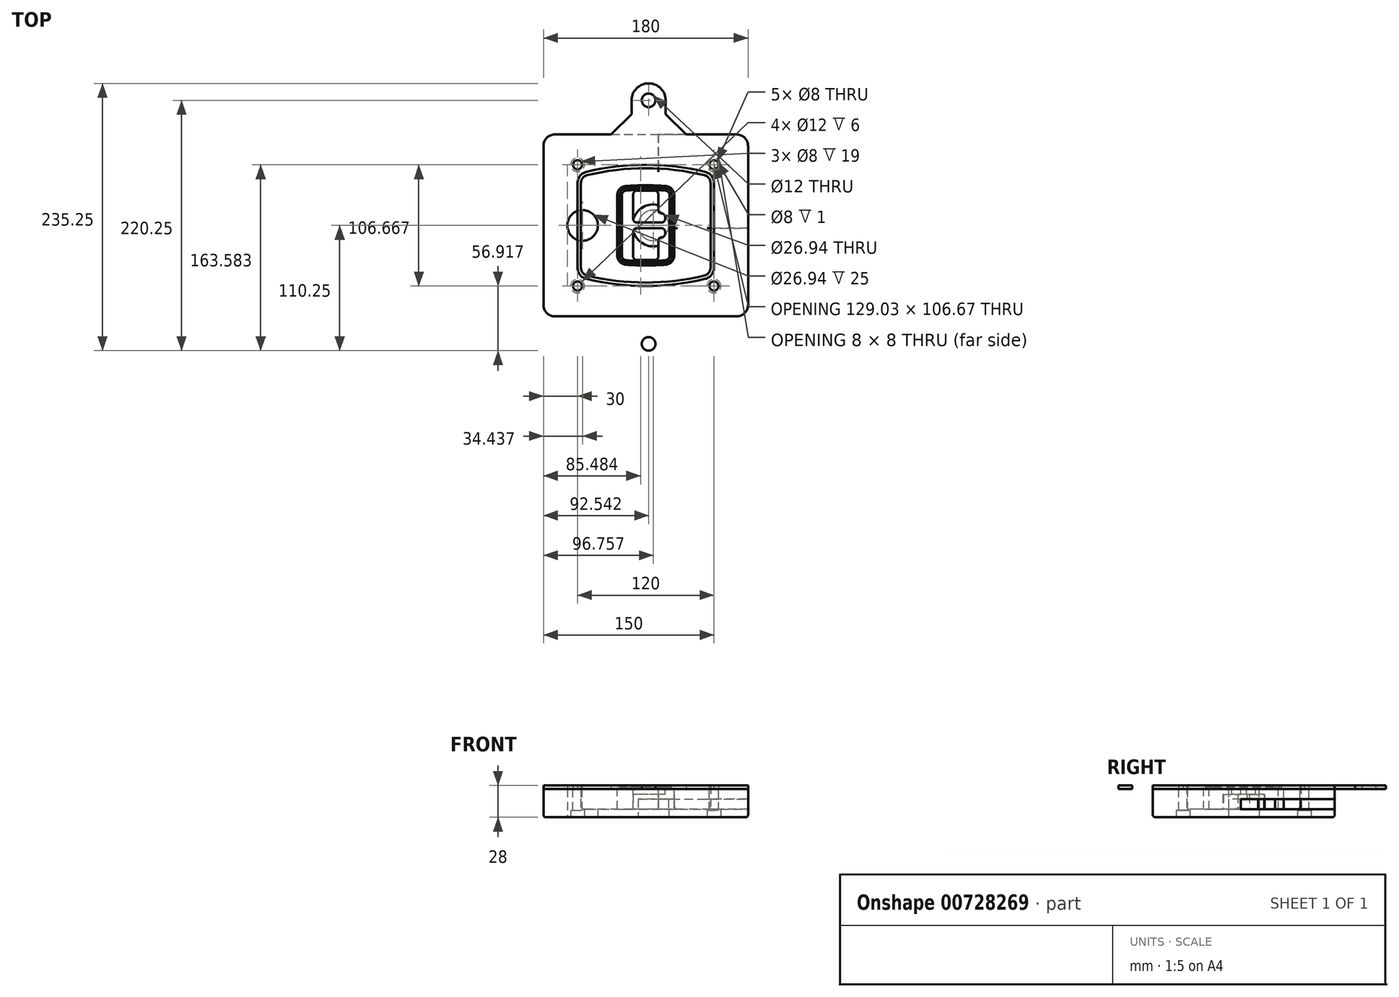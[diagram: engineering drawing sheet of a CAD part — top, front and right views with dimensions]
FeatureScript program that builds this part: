
annotation { "Feature Type Name" : "Feature", "Feature Type Description" : "" }
export const myFeature = defineFeature(function(context is Context, id is Id, definition is map)
    precondition{}
    {
        {
            var Q0;
            Q0=qCreatedBy(makeId("Top.planeOp"),FACE);
            var sketch = newSketch(context, id + "F0", { "sketchPlane" : qUnion([Q0])});
            skPoint(sketch, "E0.rect.middle", {"position": v(0, 0) * mm});
            skLineSegment(sketch, "E1.bottom", {"start": v(-80, -80) * mm, "end": v(80, -80) * mm});
            skLineSegment(sketch, "E1.top", {"start": v(-80, 80) * mm, "end": v(80, 80) * mm});
            skLineSegment(sketch, "E1.left", {"start": v(-90, -70) * mm, "end": v(-90, 70) * mm});
            skLineSegment(sketch, "E1.right", {"start": v(90, -70) * mm, "end": v(90, 70) * mm});
            skLineSegment(sketch, "E2", {"start": v(-90, 80) * mm, "end": v(90, -80) * mm, "construction": true});
            skLineSegment(sketch, "E3", {"start": v(90, 80) * mm, "end": v(-90, -80) * mm, "construction": true});
            skCircle(sketch, "E4", {"center": v(-60, 53.33) * mm, "radius": 4 * mm});
            skCircle(sketch, "E5", {"center": v(60, 53.33) * mm, "radius": 4 * mm});
            skCircle(sketch, "E6", {"center": v(60, -53.33) * mm, "radius": 4 * mm});
            skCircle(sketch, "E7", {"center": v(-60, -53.33) * mm, "radius": 4 * mm});
            skLineSegment(sketch, "E8", {"start": v(-60, 53.33) * mm, "end": v(60, 53.33) * mm, "construction": true});
            skLineSegment(sketch, "E9", {"start": v(60, 53.33) * mm, "end": v(60, -53.33) * mm, "construction": true});
            skLineSegment(sketch, "E10", {"start": v(60, -53.33) * mm, "end": v(-60, -53.33) * mm, "construction": true});
            skLineSegment(sketch, "E11", {"start": v(-60, -53.33) * mm, "end": v(-60, 53.33) * mm, "construction": true});
            skLineSegment(sketch, "E12", {"start": v(-60, 37.3) * mm, "end": v(-60, -37.3) * mm});
            skLineSegment(sketch, "E13", {"start": v(60, 37.3) * mm, "end": v(60, -37.3) * mm});
            skArc(sketch, "E14", {"start": v(52.38, 47.01) * mm, "mid": v(0, 53.33) * mm, "end": v(-52.38, 47.01) * mm});
            skArc(sketch, "E15", {"start": v(-52.38, -47.01) * mm, "mid": v(0, -53.33) * mm, "end": v(52.38, -47.01) * mm});
            skLineSegment(sketch, "E16", {"start": v(-60, 0) * mm, "end": v(60, 0) * mm, "construction": true});
            skPoint(sketch, "E17.visualSharp", {"position": v(-60, -45) * mm});
            skArc(sketch, "E17.filletArc", {"start": v(-60, -37.3) * mm, "mid": v(-57.87, -43.47) * mm, "end": v(-52.38, -47.01) * mm});
            skPoint(sketch, "E18.visualSharp", {"position": v(-60, 45) * mm});
            skArc(sketch, "E18.filletArc", {"start": v(-52.38, 47.01) * mm, "mid": v(-57.87, 43.47) * mm, "end": v(-60, 37.3) * mm});
            skPoint(sketch, "E19.visualSharp", {"position": v(60, 45) * mm});
            skArc(sketch, "E19.filletArc", {"start": v(60, 37.3) * mm, "mid": v(57.87, 43.47) * mm, "end": v(52.38, 47.01) * mm});
            skPoint(sketch, "E20.visualSharp", {"position": v(60, -45) * mm});
            skArc(sketch, "E20.filletArc", {"start": v(52.38, -47.01) * mm, "mid": v(57.87, -43.47) * mm, "end": v(60, -37.3) * mm});
            skPoint(sketch, "E21.visualSharp", {"position": v(-90, 80) * mm});
            skArc(sketch, "E21.filletArc", {"start": v(-80, 80) * mm, "mid": v(-87.07, 77.07) * mm, "end": v(-90, 70) * mm});
            skPoint(sketch, "E22.visualSharp", {"position": v(90, 80) * mm});
            skArc(sketch, "E22.filletArc", {"start": v(90, 70) * mm, "mid": v(87.07, 77.07) * mm, "end": v(80, 80) * mm});
            skPoint(sketch, "E23.visualSharp", {"position": v(90, -80) * mm});
            skArc(sketch, "E23.filletArc", {"start": v(80, -80) * mm, "mid": v(87.07, -77.07) * mm, "end": v(90, -70) * mm});
            skPoint(sketch, "E24.visualSharp", {"position": v(-90, -80) * mm});
            skArc(sketch, "E24.filletArc", {"start": v(-90, -70) * mm, "mid": v(-87.07, -77.07) * mm, "end": v(-80, -80) * mm});
            skArc(sketch, "E25.0", {"start": v(57, 37.3) * mm, "mid": v(55.5, 41.62) * mm, "end": v(51.67, 44.1) * mm});
            skLineSegment(sketch, "E25.1", {"start": v(57, 37.3) * mm, "end": v(57, -37.3) * mm});
            skArc(sketch, "E25.2", {"start": v(51.67, -44.1) * mm, "mid": v(55.5, -41.62) * mm, "end": v(57, -37.3) * mm});
            skArc(sketch, "E25.3", {"start": v(-51.67, -44.1) * mm, "mid": v(0, -50.33) * mm, "end": v(51.67, -44.1) * mm});
            skArc(sketch, "E25.4", {"start": v(-57, -37.3) * mm, "mid": v(-55.5, -41.62) * mm, "end": v(-51.67, -44.1) * mm});
            skArc(sketch, "E25.5", {"start": v(51.67, 44.1) * mm, "mid": v(0, 50.33) * mm, "end": v(-51.67, 44.1) * mm});
            skLineSegment(sketch, "E25.6", {"start": v(-57, 37.3) * mm, "end": v(-57, -37.3) * mm});
            skArc(sketch, "E25.7", {"start": v(-51.67, 44.1) * mm, "mid": v(-55.5, 41.62) * mm, "end": v(-57, 37.3) * mm});
            skArc(sketch, "E26.0", {"start": v(-53.33, 50.9) * mm, "mid": v(-61.01, 45.94) * mm, "end": v(-64, 37.3) * mm});
            skArc(sketch, "E26.1", {"start": v(53.33, 50.9) * mm, "mid": v(0, 57.33) * mm, "end": v(-53.33, 50.9) * mm});
            skArc(sketch, "E26.2", {"start": v(64, 37.3) * mm, "mid": v(61.01, 45.94) * mm, "end": v(53.33, 50.9) * mm});
            skLineSegment(sketch, "E26.3", {"start": v(64, 37.3) * mm, "end": v(64, -37.3) * mm});
            skArc(sketch, "E26.4", {"start": v(53.33, -50.9) * mm, "mid": v(61.01, -45.94) * mm, "end": v(64, -37.3) * mm});
            skLineSegment(sketch, "E26.5", {"start": v(-64, 37.3) * mm, "end": v(-64, -37.3) * mm});
            skArc(sketch, "E26.6", {"start": v(-53.33, -50.9) * mm, "mid": v(0, -57.33) * mm, "end": v(53.33, -50.9) * mm});
            skArc(sketch, "E26.7", {"start": v(-64, -37.3) * mm, "mid": v(-61.01, -45.94) * mm, "end": v(-53.33, -50.9) * mm});
            skSolve(sketch);
        }
        {
            var Q0;
            Q0=makeQuery(id+"F0.imprint","IMPRINT",FACE,{"disambiguationData":[TD([[makeQuery(id+"F0.imprint","IMPRINT",EDGE,{"derivedFrom":sQuery(id+"F0.wireOp",EDGE,"E1.bottom")}),1.0]])]});
            var Q1;
            Q1=makeQuery(id+"F0.imprint","IMPRINT",FACE,{"disambiguationData":[TD([[makeQuery(id+"F0.imprint","IMPRINT",EDGE,{"derivedFrom":sQuery(id+"F0.wireOp",EDGE,"E12")}),1.0]])]});
            var Q2;
            Q2=makeQuery(id+"F0.imprint","IMPRINT",FACE,{"disambiguationData":[TD([[makeQuery(id+"F0.imprint","IMPRINT",EDGE,{"derivedFrom":sQuery(id+"F0.wireOp",EDGE,"E25.0")}),1.0]])]});
            var Q3;
            Q3=makeQuery(id+"F0.imprint","IMPRINT",FACE,{"disambiguationData":[TD([[makeQuery(id+"F0.imprint","IMPRINT",EDGE,{"derivedFrom":sQuery(id+"F0.wireOp",EDGE,"E12")}),-1.0]])]});
            extrude(context, id + "F1", {"entities" : qUnion([Q0, Q1, Q2, Q3]), "oppositeDirection" : true, "depth" : 25 * mm, "offsetDistance" : 25 * mm});
        }
        {
            var Q0;
            Q0=makeQuery(id+"F0.imprint","IMPRINT",FACE,{"disambiguationData":[TD([[makeQuery(id+"F0.imprint","IMPRINT",EDGE,{"derivedFrom":sQuery(id+"F0.wireOp",EDGE,"E12")}),1.0]])]});
            extrude(context, id + "F2", {"entities" : qUnion([Q0]), "operationType" : NewBodyOperationType.ADD, "depth" : 3 * mm});
        }
        {
            var Q0;
            Q0=makeQuery(id+"F0.imprint","IMPRINT",FACE,{"disambiguationData":[TD([[makeQuery(id+"F0.imprint","IMPRINT",EDGE,{"derivedFrom":sQuery(id+"F0.wireOp",EDGE,"E25.0")}),1.0]])]});
            extrude(context, id + "F3", {"entities" : qUnion([Q0]), "operationType" : NewBodyOperationType.REMOVE, "oppositeDirection" : true, "depth" : 18 * mm});
        }
        {
            var Q0;
            Q0=makeQuery(id+"F2.opExtrude","CAP_FACE",FACE,{"disambiguationData":[OSD([sQuery(id+"F0.wireOp",EDGE,"E12"),sQuery(id+"F0.wireOp",EDGE,"E13"),sQuery(id+"F0.wireOp",EDGE,"E14"),sQuery(id+"F0.wireOp",EDGE,"E15"),sQuery(id+"F0.wireOp",EDGE,"E17.filletArc"),sQuery(id+"F0.wireOp",EDGE,"E18.filletArc"),sQuery(id+"F0.wireOp",EDGE,"E19.filletArc"),sQuery(id+"F0.wireOp",EDGE,"E20.filletArc"),sQuery(id+"F0.wireOp",EDGE,"E25.0"),sQuery(id+"F0.wireOp",EDGE,"E25.1"),sQuery(id+"F0.wireOp",EDGE,"E25.2"),sQuery(id+"F0.wireOp",EDGE,"E25.3"),sQuery(id+"F0.wireOp",EDGE,"E25.4"),sQuery(id+"F0.wireOp",EDGE,"E25.5"),sQuery(id+"F0.wireOp",EDGE,"E25.6"),sQuery(id+"F0.wireOp",EDGE,"E25.7")])],"isStart":false});
            var sketch = newSketch(context, id + "F4", { "sketchPlane" : qUnion([Q0])});
            skArc(sketch, "E27.0", {"start": v(-17.7, -34.56) * mm, "mid": v(0, -35.33) * mm, "end": v(17.7, -34.56) * mm});
            skArc(sketch, "E28.0", {"start": v(17.7, 34.56) * mm, "mid": v(0, 35.33) * mm, "end": v(-17.7, 34.56) * mm});
            skLineSegment(sketch, "E29", {"start": v(-25, 26.59) * mm, "end": v(-25, -26.59) * mm});
            skLineSegment(sketch, "E30", {"start": v(25, 26.59) * mm, "end": v(25, -26.59) * mm});
            skLineSegment(sketch, "E31", {"start": v(-25, 33.78) * mm, "end": v(25, 33.78) * mm, "construction": true});
            skLineSegment(sketch, "E32", {"start": v(-25, -33.78) * mm, "end": v(25, -33.78) * mm, "construction": true});
            skPoint(sketch, "E33.visualSharp", {"position": v(-25, 33.78) * mm});
            skArc(sketch, "E33.filletArc", {"start": v(-17.7, 34.56) * mm, "mid": v(-22.9, 32) * mm, "end": v(-25, 26.59) * mm});
            skPoint(sketch, "E34.visualSharp", {"position": v(25, 33.78) * mm});
            skArc(sketch, "E34.filletArc", {"start": v(25, 26.59) * mm, "mid": v(22.9, 32) * mm, "end": v(17.7, 34.56) * mm});
            skPoint(sketch, "E35.visualSharp", {"position": v(25, -33.78) * mm});
            skArc(sketch, "E35.filletArc", {"start": v(17.7, -34.56) * mm, "mid": v(22.9, -32) * mm, "end": v(25, -26.59) * mm});
            skPoint(sketch, "E36.visualSharp", {"position": v(-25, -33.78) * mm});
            skArc(sketch, "E36.filletArc", {"start": v(-25, -26.59) * mm, "mid": v(-22.9, -32) * mm, "end": v(-17.7, -34.56) * mm});
            skArc(sketch, "E37.0", {"start": v(51.67, 44.1) * mm, "mid": v(0, 50.33) * mm, "end": v(-51.67, 44.1) * mm});
            skArc(sketch, "E37.1", {"start": v(-51.67, 44.1) * mm, "mid": v(-55.5, 41.62) * mm, "end": v(-57, 37.3) * mm});
            skLineSegment(sketch, "E37.2", {"start": v(-57, 37.3) * mm, "end": v(-57, -37.3) * mm});
            skArc(sketch, "E37.3", {"start": v(-57, -37.3) * mm, "mid": v(-55.5, -41.62) * mm, "end": v(-51.67, -44.1) * mm});
            skArc(sketch, "E37.4", {"start": v(-51.67, -44.1) * mm, "mid": v(0, -50.33) * mm, "end": v(51.67, -44.1) * mm});
            skArc(sketch, "E37.5", {"start": v(51.67, -44.1) * mm, "mid": v(55.5, -41.62) * mm, "end": v(57, -37.3) * mm});
            skLineSegment(sketch, "E37.6", {"start": v(57, 37.3) * mm, "end": v(57, -37.3) * mm});
            skArc(sketch, "E37.7", {"start": v(57, 37.3) * mm, "mid": v(55.5, 41.62) * mm, "end": v(51.67, 44.1) * mm});
            skLineSegment(sketch, "E38.0", {"start": v(23, 26.59) * mm, "end": v(23, -26.59) * mm});
            skArc(sketch, "E38.1", {"start": v(17.53, -32.56) * mm, "mid": v(21.42, -30.64) * mm, "end": v(23, -26.59) * mm});
            skArc(sketch, "E38.2", {"start": v(-17.53, -32.56) * mm, "mid": v(0, -33.33) * mm, "end": v(17.53, -32.56) * mm});
            skArc(sketch, "E38.3", {"start": v(-23, -26.59) * mm, "mid": v(-21.42, -30.64) * mm, "end": v(-17.53, -32.56) * mm});
            skLineSegment(sketch, "E38.4", {"start": v(-23, 26.59) * mm, "end": v(-23, -26.59) * mm});
            skArc(sketch, "E38.5", {"start": v(23, 26.59) * mm, "mid": v(21.42, 30.64) * mm, "end": v(17.53, 32.56) * mm});
            skArc(sketch, "E38.6", {"start": v(-17.53, 32.56) * mm, "mid": v(-21.42, 30.64) * mm, "end": v(-23, 26.59) * mm});
            skArc(sketch, "E38.7", {"start": v(17.53, 32.56) * mm, "mid": v(0, 33.33) * mm, "end": v(-17.53, 32.56) * mm});
            skArc(sketch, "E39.0", {"start": v(21, 26.59) * mm, "mid": v(19.95, 29.29) * mm, "end": v(17.35, 30.57) * mm});
            skLineSegment(sketch, "E39.1", {"start": v(21, 26.59) * mm, "end": v(21, -26.59) * mm});
            skArc(sketch, "E39.2", {"start": v(17.35, -30.57) * mm, "mid": v(19.95, -29.29) * mm, "end": v(21, -26.59) * mm});
            skArc(sketch, "E39.3", {"start": v(-17.35, -30.57) * mm, "mid": v(0, -31.33) * mm, "end": v(17.35, -30.57) * mm});
            skArc(sketch, "E39.4", {"start": v(-21, -26.59) * mm, "mid": v(-19.95, -29.29) * mm, "end": v(-17.35, -30.57) * mm});
            skArc(sketch, "E39.5", {"start": v(17.35, 30.57) * mm, "mid": v(0, 31.33) * mm, "end": v(-17.35, 30.57) * mm});
            skLineSegment(sketch, "E39.6", {"start": v(-21, 26.59) * mm, "end": v(-21, -26.59) * mm});
            skArc(sketch, "E39.7", {"start": v(-17.35, 30.57) * mm, "mid": v(-19.95, 29.29) * mm, "end": v(-21, 26.59) * mm});
            skLineSegment(sketch, "E40", {"start": v(-25, 0) * mm, "end": v(25, 0) * mm, "construction": true});
            skLineSegment(sketch, "E41", {"start": v(-11, 5.5) * mm, "end": v(-11, 27.5) * mm});
            skLineSegment(sketch, "E42", {"start": v(-8, 30.5) * mm, "end": v(8, 30.5) * mm});
            skLineSegment(sketch, "E43", {"start": v(11, 27.5) * mm, "end": v(11, 13.5) * mm});
            skLineSegment(sketch, "E44", {"start": v(14, 10.5) * mm, "end": v(14, 10.5) * mm});
            skLineSegment(sketch, "E45", {"start": v(17, 7.5) * mm, "end": v(17, 5.5) * mm});
            skLineSegment(sketch, "E46", {"start": v(14, 2.5) * mm, "end": v(-8, 2.5) * mm});
            skPoint(sketch, "E47.visualSharp", {"position": v(-11, 30.5) * mm});
            skArc(sketch, "E47.filletArc", {"start": v(-8, 30.5) * mm, "mid": v(-10.12, 29.62) * mm, "end": v(-11, 27.5) * mm});
            skPoint(sketch, "E48.visualSharp", {"position": v(11, 30.5) * mm});
            skArc(sketch, "E48.filletArc", {"start": v(11, 27.5) * mm, "mid": v(10.12, 29.62) * mm, "end": v(8, 30.5) * mm});
            skPoint(sketch, "E49.visualSharp", {"position": v(11, 10.5) * mm});
            skArc(sketch, "E49.filletArc", {"start": v(11, 13.5) * mm, "mid": v(11.88, 11.38) * mm, "end": v(14, 10.5) * mm});
            skPoint(sketch, "E50.visualSharp", {"position": v(17, 10.5) * mm});
            skArc(sketch, "E50.filletArc", {"start": v(17, 7.5) * mm, "mid": v(16.12, 9.62) * mm, "end": v(14, 10.5) * mm});
            skPoint(sketch, "E51.visualSharp", {"position": v(17, 2.5) * mm});
            skArc(sketch, "E51.filletArc", {"start": v(14, 2.5) * mm, "mid": v(16.12, 3.38) * mm, "end": v(17, 5.5) * mm});
            skPoint(sketch, "E52.visualSharp", {"position": v(-11, 2.5) * mm});
            skArc(sketch, "E52.filletArc", {"start": v(-11, 5.5) * mm, "mid": v(-10.12, 3.38) * mm, "end": v(-8, 2.5) * mm});
            skLineSegment(sketch, "E53.0.MirrorCS", {"start": v(14, -2.5) * mm, "end": v(-8, -2.5) * mm});
            skArc(sketch, "E54.0.MirrorCS", {"start": v(-11, -5.5) * mm, "mid": v(-10.12, -3.38) * mm, "end": v(-8, -2.5) * mm});
            skLineSegment(sketch, "E55.0.MirrorCS", {"start": v(-11, -5.5) * mm, "end": v(-11, -27.5) * mm});
            skArc(sketch, "E56.0.MirrorCS", {"start": v(-8, -30.5) * mm, "mid": v(-10.12, -29.62) * mm, "end": v(-11, -27.5) * mm});
            skLineSegment(sketch, "E57.0.MirrorCS", {"start": v(-8, -30.5) * mm, "end": v(8, -30.5) * mm});
            skArc(sketch, "E58.0.MirrorCS", {"start": v(11, -27.5) * mm, "mid": v(10.12, -29.62) * mm, "end": v(8, -30.5) * mm});
            skLineSegment(sketch, "E59.0.MirrorCS", {"start": v(11, -27.5) * mm, "end": v(11, -13.5) * mm});
            skArc(sketch, "E60.0.MirrorCS", {"start": v(11, -13.5) * mm, "mid": v(11.88, -11.38) * mm, "end": v(14, -10.5) * mm});
            skArc(sketch, "E61.0.MirrorCS", {"start": v(17, -7.5) * mm, "mid": v(16.12, -9.62) * mm, "end": v(14, -10.5) * mm});
            skLineSegment(sketch, "E62.0.MirrorCS", {"start": v(17, -7.5) * mm, "end": v(17, -5.5) * mm});
            skArc(sketch, "E63.0.MirrorCS", {"start": v(14, -2.5) * mm, "mid": v(16.12, -3.38) * mm, "end": v(17, -5.5) * mm});
            skSolve(sketch);
        }
        {
            var Q0;
            Q0=makeQuery(id+"F4.imprint","IMPRINT",FACE,{"disambiguationData":[TD([[makeQuery(id+"F4.imprint","IMPRINT",EDGE,{"derivedFrom":sQuery(id+"F4.wireOp",EDGE,"E27.0")}),1.0]])]});
            var Q1;
            Q1=makeQuery(id+"F4.imprint","IMPRINT",FACE,{"disambiguationData":[TD([[makeQuery(id+"F4.imprint","IMPRINT",EDGE,{"derivedFrom":sQuery(id+"F4.wireOp",EDGE,"E38.0")}),-1.0]])]});
            var Q2;
            Q2=makeQuery(id+"F4.imprint","IMPRINT",FACE,{"disambiguationData":[TD([[makeQuery(id+"F4.imprint","IMPRINT",EDGE,{"derivedFrom":sQuery(id+"F4.wireOp",EDGE,"E39.0")}),1.0]])]});
            extrude(context, id + "F5", {"entities" : qUnion([Q0, Q1, Q2]), "operationType" : NewBodyOperationType.ADD, "endBound" : BoundingType.UP_TO_NEXT, "oppositeDirection" : true, "depth" : 25 * mm});
        }
        {
            var Q0;
            Q0=makeQuery(id+"F4.imprint","IMPRINT",FACE,{"disambiguationData":[TD([[makeQuery(id+"F4.imprint","IMPRINT",EDGE,{"derivedFrom":sQuery(id+"F4.wireOp",EDGE,"E38.0")}),-1.0]])]});
            extrude(context, id + "F6", {"entities" : qUnion([Q0]), "operationType" : NewBodyOperationType.REMOVE, "oppositeDirection" : true, "depth" : 2 * mm});
        }
        {
            var Q0;
            Q0=makeQuery(id+"F1.opExtrude","CAP_FACE",FACE,{"disambiguationData":[OSD([sQuery(id+"F0.wireOp",EDGE,"E1.bottom"),sQuery(id+"F0.wireOp",EDGE,"E1.top"),sQuery(id+"F0.wireOp",EDGE,"E1.left"),sQuery(id+"F0.wireOp",EDGE,"E1.right"),sQuery(id+"F0.wireOp",EDGE,"E4"),sQuery(id+"F0.wireOp",EDGE,"E5"),sQuery(id+"F0.wireOp",EDGE,"E6"),sQuery(id+"F0.wireOp",EDGE,"E7"),sQuery(id+"F0.wireOp",EDGE,"E21.filletArc"),sQuery(id+"F0.wireOp",EDGE,"E22.filletArc"),sQuery(id+"F0.wireOp",EDGE,"E23.filletArc"),sQuery(id+"F0.wireOp",EDGE,"E24.filletArc")])],"isStart":false});
            var sketch = newSketch(context, id + "F7", { "sketchPlane" : qUnion([Q0])});
            skCircle(sketch, "E64", {"center": v(6.76, 0) * mm, "radius": 13.47 * mm});
            skCircle(sketch, "E65", {"center": v(-55.56, 0) * mm, "radius": 13.47 * mm});
            skLineSegment(sketch, "E66", {"start": v(90, 0) * mm, "end": v(-90, 0) * mm});
            skCircle(sketch, "E67", {"center": v(6.76, 0) * mm, "radius": 18.47 * mm});
            skCircle(sketch, "E68", {"center": v(60, -53.33) * mm, "radius": 6 * mm});
            skCircle(sketch, "E69", {"center": v(-60, -53.33) * mm, "radius": 6 * mm});
            skCircle(sketch, "E70", {"center": v(-60, 53.33) * mm, "radius": 6 * mm});
            skCircle(sketch, "E71", {"center": v(60, 53.33) * mm, "radius": 6 * mm});
            skSolve(sketch);
        }
        {
            var Q0;
            {var subQ1=sQuery(id+"F7.wireOp",EDGE,"E66");var subQ4=sQuery(id+"F7.wireOp",EDGE,"E64");var subQ6=makeQuery(id+"F7.imprint","INTERSECT",VERTEX,{"disambiguationData":[OD(0.0)],"derivedFrom":[subQ4,subQ1]});Q0=makeQuery(id+"F7.imprint","IMPRINT",FACE,{"disambiguationData":[TD([[makeQuery(id+"F7.imprint","IMPRINT",EDGE,{"disambiguationData":[TD([[subQ6,-1.0]])],"derivedFrom":subQ4}),-1.0]])]});}
            var Q1;
            {var subQ0=sQuery(id+"F7.wireOp",EDGE,"E66");var subQ1=sQuery(id+"F7.wireOp",EDGE,"E64");var subQ3=makeQuery(id+"F7.imprint","INTERSECT",VERTEX,{"disambiguationData":[OD(0.0)],"derivedFrom":[subQ1,subQ0]});Q1=makeQuery(id+"F7.imprint","IMPRINT",FACE,{"disambiguationData":[TD([[makeQuery(id+"F7.imprint","IMPRINT",EDGE,{"disambiguationData":[TD([[subQ3,-1.0]])],"derivedFrom":subQ1}),1.0]])]});}
            var Q2;
            {var subQ0=sQuery(id+"F7.wireOp",EDGE,"E66");var subQ1=sQuery(id+"F7.wireOp",EDGE,"E64");var subQ3=makeQuery(id+"F7.imprint","INTERSECT",VERTEX,{"disambiguationData":[OD(0.0)],"derivedFrom":[subQ1,subQ0]});Q2=makeQuery(id+"F7.imprint","IMPRINT",FACE,{"disambiguationData":[TD([[makeQuery(id+"F7.imprint","IMPRINT",EDGE,{"disambiguationData":[TD([[subQ3,1.0]])],"derivedFrom":subQ1}),1.0]])]});}
            var Q3;
            {var subQ1=sQuery(id+"F7.wireOp",EDGE,"E66");var subQ4=sQuery(id+"F7.wireOp",EDGE,"E64");var subQ6=makeQuery(id+"F7.imprint","INTERSECT",VERTEX,{"disambiguationData":[OD(0.0)],"derivedFrom":[subQ4,subQ1]});Q3=makeQuery(id+"F7.imprint","IMPRINT",FACE,{"disambiguationData":[TD([[makeQuery(id+"F7.imprint","IMPRINT",EDGE,{"disambiguationData":[TD([[subQ6,1.0]])],"derivedFrom":subQ4}),-1.0]])]});}
            extrude(context, id + "F8", {"entities" : qUnion([Q0, Q1, Q2, Q3]), "operationType" : NewBodyOperationType.ADD, "oppositeDirection" : true, "depth" : 20 * mm});
        }
        {
            var Q0;
            {var subQ0=sQuery(id+"F7.wireOp",EDGE,"E66");var subQ1=sQuery(id+"F7.wireOp",EDGE,"E64");var subQ3=makeQuery(id+"F7.imprint","INTERSECT",VERTEX,{"disambiguationData":[OD(0.0)],"derivedFrom":[subQ1,subQ0]});Q0=makeQuery(id+"F7.imprint","IMPRINT",FACE,{"disambiguationData":[TD([[makeQuery(id+"F7.imprint","IMPRINT",EDGE,{"disambiguationData":[TD([[subQ3,-1.0]])],"derivedFrom":subQ1}),1.0]])]});}
            var Q1;
            {var subQ0=sQuery(id+"F7.wireOp",EDGE,"E66");var subQ1=sQuery(id+"F7.wireOp",EDGE,"E64");var subQ3=makeQuery(id+"F7.imprint","INTERSECT",VERTEX,{"disambiguationData":[OD(0.0)],"derivedFrom":[subQ1,subQ0]});Q1=makeQuery(id+"F7.imprint","IMPRINT",FACE,{"disambiguationData":[TD([[makeQuery(id+"F7.imprint","IMPRINT",EDGE,{"disambiguationData":[TD([[subQ3,1.0]])],"derivedFrom":subQ1}),1.0]])]});}
            extrude(context, id + "F9", {"entities" : qUnion([Q0, Q1]), "operationType" : NewBodyOperationType.REMOVE, "oppositeDirection" : true, "depth" : 16 * mm});
        }
        {
            var Q0;
            {var subQ0=sQuery(id+"F7.wireOp",EDGE,"E66");var subQ1=sQuery(id+"F7.wireOp",EDGE,"E65");var subQ3=makeQuery(id+"F7.imprint","INTERSECT",VERTEX,{"disambiguationData":[OD(0.0)],"derivedFrom":[subQ1,subQ0]});Q0=makeQuery(id+"F7.imprint","IMPRINT",FACE,{"disambiguationData":[TD([[makeQuery(id+"F7.imprint","IMPRINT",EDGE,{"disambiguationData":[TD([[subQ3,-1.0]])],"derivedFrom":subQ1}),1.0]])]});}
            var Q1;
            {var subQ0=sQuery(id+"F7.wireOp",EDGE,"E66");var subQ1=sQuery(id+"F7.wireOp",EDGE,"E65");var subQ3=makeQuery(id+"F7.imprint","INTERSECT",VERTEX,{"disambiguationData":[OD(0.0)],"derivedFrom":[subQ1,subQ0]});Q1=makeQuery(id+"F7.imprint","IMPRINT",FACE,{"disambiguationData":[TD([[makeQuery(id+"F7.imprint","IMPRINT",EDGE,{"disambiguationData":[TD([[subQ3,1.0]])],"derivedFrom":subQ1}),1.0]])]});}
            extrude(context, id + "F10", {"entities" : qUnion([Q0, Q1]), "operationType" : NewBodyOperationType.REMOVE, "oppositeDirection" : true, "depth" : 25 * mm});
        }
        {
            var Q0;
            Q0=makeQuery(id+"F7.imprint","IMPRINT",FACE,{"disambiguationData":[TD([[makeQuery(id+"F7.imprint","IMPRINT",EDGE,{"derivedFrom":sQuery(id+"F7.wireOp",EDGE,"E68")}),1.0]])]});
            var Q1;
            Q1=makeQuery(id+"F7.imprint","IMPRINT",FACE,{"disambiguationData":[TD([[makeQuery(id+"F7.imprint","IMPRINT",EDGE,{"derivedFrom":makeQuery(id+"F1.opExtrude","CAP_EDGE",EDGE,{"disambiguationData":[OSD([sQuery(id+"F0.wireOp",EDGE,"E5")])],"isStart":false})}),-1.0]])]});
            var Q2;
            Q2=makeQuery(id+"F7.imprint","IMPRINT",FACE,{"disambiguationData":[TD([[makeQuery(id+"F7.imprint","IMPRINT",EDGE,{"derivedFrom":sQuery(id+"F7.wireOp",EDGE,"E69")}),1.0]])]});
            var Q3;
            Q3=makeQuery(id+"F7.imprint","IMPRINT",FACE,{"disambiguationData":[TD([[makeQuery(id+"F7.imprint","IMPRINT",EDGE,{"derivedFrom":makeQuery(id+"F1.opExtrude","CAP_EDGE",EDGE,{"disambiguationData":[OSD([sQuery(id+"F0.wireOp",EDGE,"E4")])],"isStart":false})}),-1.0]])]});
            var Q4;
            Q4=makeQuery(id+"F7.imprint","IMPRINT",FACE,{"disambiguationData":[TD([[makeQuery(id+"F7.imprint","IMPRINT",EDGE,{"derivedFrom":sQuery(id+"F7.wireOp",EDGE,"E70")}),1.0]])]});
            var Q5;
            Q5=makeQuery(id+"F7.imprint","IMPRINT",FACE,{"disambiguationData":[TD([[makeQuery(id+"F7.imprint","IMPRINT",EDGE,{"derivedFrom":makeQuery(id+"F1.opExtrude","CAP_EDGE",EDGE,{"disambiguationData":[OSD([sQuery(id+"F0.wireOp",EDGE,"E7")])],"isStart":false})}),-1.0]])]});
            var Q6;
            Q6=makeQuery(id+"F7.imprint","IMPRINT",FACE,{"disambiguationData":[TD([[makeQuery(id+"F7.imprint","IMPRINT",EDGE,{"derivedFrom":sQuery(id+"F7.wireOp",EDGE,"E71")}),1.0]])]});
            var Q7;
            Q7=makeQuery(id+"F7.imprint","IMPRINT",FACE,{"disambiguationData":[TD([[makeQuery(id+"F7.imprint","IMPRINT",EDGE,{"derivedFrom":makeQuery(id+"F1.opExtrude","CAP_EDGE",EDGE,{"disambiguationData":[OSD([sQuery(id+"F0.wireOp",EDGE,"E6")])],"isStart":false})}),-1.0]])]});
            extrude(context, id + "F11", {"entities" : qUnion([Q0, Q1, Q2, Q3, Q4, Q5, Q6, Q7]), "operationType" : NewBodyOperationType.REMOVE, "oppositeDirection" : true, "depth" : 6 * mm});
        }
        {
            var Q0;
            Q0=makeQuery(id+"F9.boolean.opBoolean","COPY",FACE,{"derivedFrom":makeQuery(id+"F9.opExtrude","CAP_FACE",FACE,{"disambiguationData":[OSD([sQuery(id+"F7.wireOp",EDGE,"E64")])],"isStart":false})});
            var sketch = newSketch(context, id + "F12", { "sketchPlane" : qUnion([Q0])});
            skArc(sketch, "E72.0", {"start": v(11, -88.19) * mm, "mid": v(97.1, -83.6) * mm, "end": v(92.5, 2.5) * mm});
            skLineSegment(sketch, "E72.1", {"start": v(11, -17.97) * mm, "end": v(11, -17.97) * mm});
            skLineSegment(sketch, "E73", {"start": v(92.5, -105.13) * mm, "end": v(102.3, -105.13) * mm});
            skLineSegment(sketch, "E74.0", {"start": v(92.5, 2.5) * mm, "end": v(14, 2.5) * mm});
            skArc(sketch, "E74.1", {"start": v(14, 2.5) * mm, "mid": v(16.12, 3.38) * mm, "end": v(17, 5.5) * mm});
            skLineSegment(sketch, "E74.2", {"start": v(17, 7.5) * mm, "end": v(17, 5.5) * mm});
            skArc(sketch, "E74.3", {"start": v(17, 7.5) * mm, "mid": v(16.12, 9.62) * mm, "end": v(14, 10.5) * mm});
            skArc(sketch, "E74.4", {"start": v(11, 13.5) * mm, "mid": v(11.88, 11.38) * mm, "end": v(14, 10.5) * mm});
            skLineSegment(sketch, "E74.5", {"start": v(11, 13.5) * mm, "end": v(11, -88.19) * mm});
            skLineSegment(sketch, "E74.7", {"start": v(92.5, -2.5) * mm, "end": v(14, -2.5) * mm});
            skArc(sketch, "E74.8", {"start": v(14, -2.5) * mm, "mid": v(16.12, -3.38) * mm, "end": v(17, -5.5) * mm});
            skLineSegment(sketch, "E74.9", {"start": v(17, -7.5) * mm, "end": v(17, -5.5) * mm});
            skArc(sketch, "E74.10", {"start": v(17, -7.5) * mm, "mid": v(16.12, -9.62) * mm, "end": v(14, -10.5) * mm});
            skArc(sketch, "E74.11", {"start": v(11, -13.5) * mm, "mid": v(11.88, -11.38) * mm, "end": v(14, -10.5) * mm});
            skLineSegment(sketch, "E74.12", {"start": v(11, -17.97) * mm, "end": v(11, -13.5) * mm});
            skPoint(sketch, "E75.orphan", {"position": v(11, -27.5) * mm});
            skPoint(sketch, "E76.orphan", {"position": v(-8, -2.5) * mm});
            skPoint(sketch, "E77.orphan", {"position": v(-8, 2.5) * mm});
            skPoint(sketch, "E78.orphan", {"position": v(11, 27.5) * mm});
            skSolve(sketch);
        }
        {
            var Q0;
            {var subQ7=sQuery(id+"F12.wireOp",EDGE,"E72.0");var subQ14=sQuery(id+"F12.wireOp",EDGE,"E72.1");var subQ16=sQuery(id+"F12.wireOp",EDGE,"E74.1");var subQ18=sQuery(id+"F12.wireOp",EDGE,"E74.8");Q0=qUnion([makeQuery(id+"F12.imprint","IMPRINT",FACE,{"disambiguationData":[TD([[makeQuery(id+"F12.imprint","IMPRINT",EDGE,{"derivedFrom":subQ7}),1.0]])]}),makeQuery(id+"F12.imprint","IMPRINT",FACE,{"disambiguationData":[TD([[makeQuery(id+"F12.imprint","IMPRINT",EDGE,{"derivedFrom":subQ14}),1.0]])]}),makeQuery(id+"F12.imprint","IMPRINT",FACE,{"disambiguationData":[TD([[makeQuery(id+"F12.imprint","IMPRINT",EDGE,{"derivedFrom":subQ16}),1.0]])]}),makeQuery(id+"F12.imprint","IMPRINT",FACE,{"disambiguationData":[TD([[makeQuery(id+"F12.imprint","IMPRINT",EDGE,{"derivedFrom":subQ18}),-1.0]])]})]);}
            var Q1;
            Q1=makeQuery(id+"F5.boolean.opBoolean","SPLIT",FACE,{"disambiguationData":[TD([makeQuery(id+"F5.opExtrude","SWEPT_FACE",FACE,{"disambiguationData":[OSD([sQuery(id+"F4.wireOp",EDGE,"E41")])]})])],"derivedFrom":makeQuery(id+"F3.boolean.opBoolean","COPY",FACE,{"derivedFrom":makeQuery(id+"F3.opExtrude","CAP_FACE",FACE,{"disambiguationData":[OSD([sQuery(id+"F0.wireOp",EDGE,"E25.0"),sQuery(id+"F0.wireOp",EDGE,"E25.1"),sQuery(id+"F0.wireOp",EDGE,"E25.2"),sQuery(id+"F0.wireOp",EDGE,"E25.3"),sQuery(id+"F0.wireOp",EDGE,"E25.4"),sQuery(id+"F0.wireOp",EDGE,"E25.5"),sQuery(id+"F0.wireOp",EDGE,"E25.6"),sQuery(id+"F0.wireOp",EDGE,"E25.7")])],"isStart":false})})});
            extrude(context, id + "F13", {"entities" : qUnion([Q0]), "operationType" : NewBodyOperationType.REMOVE, "endBound" : BoundingType.UP_TO_SURFACE, "endBoundEntityFace" : qUnion([Q1]), "depth" : 25 * mm});
        }
        {
            var Q0;
            Q0=makeQuery(id+"F3.boolean.opBoolean","COPY",EDGE,{"derivedFrom":makeQuery(id+"F3.opExtrude","CAP_EDGE",EDGE,{"disambiguationData":[OSD([sQuery(id+"F0.wireOp",EDGE,"E25.6")])],"isStart":false})});
            var Q1;
            Q1=makeQuery(id+"F8.boolean.opBoolean","INTERSECT",EDGE,{"derivedFrom":[makeQuery(id+"F5.opExtrude","SWEPT_FACE",FACE,{"disambiguationData":[OSD([sQuery(id+"F4.wireOp",EDGE,"E30")])]}),makeQuery(id+"F8.opExtrude","CAP_FACE",FACE,{"disambiguationData":[OSD([sQuery(id+"F7.wireOp",EDGE,"E67")])],"isStart":false})]});
            var Q2;
            Q2=makeQuery(id+"F8.boolean.opBoolean","INTERSECT",EDGE,{"disambiguationData":[OD(1.0)],"derivedFrom":[makeQuery(id+"F5.opExtrude","SWEPT_FACE",FACE,{"disambiguationData":[OSD([sQuery(id+"F4.wireOp",EDGE,"E30")])]}),makeQuery(id+"F8.opExtrude","SWEPT_FACE",FACE,{"disambiguationData":[OSD([sQuery(id+"F7.wireOp",EDGE,"E67")])]})]});
            var Q3;
            {var subQ0=makeQuery(id+"F3.boolean.opBoolean","COPY",FACE,{"derivedFrom":makeQuery(id+"F3.opExtrude","CAP_FACE",FACE,{"disambiguationData":[OSD([sQuery(id+"F0.wireOp",EDGE,"E25.0"),sQuery(id+"F0.wireOp",EDGE,"E25.1"),sQuery(id+"F0.wireOp",EDGE,"E25.2"),sQuery(id+"F0.wireOp",EDGE,"E25.3"),sQuery(id+"F0.wireOp",EDGE,"E25.4"),sQuery(id+"F0.wireOp",EDGE,"E25.5"),sQuery(id+"F0.wireOp",EDGE,"E25.6"),sQuery(id+"F0.wireOp",EDGE,"E25.7")])],"isStart":false})});var subQ1=sQuery(id+"F4.wireOp",EDGE,"E30");Q3=makeQuery(id+"F8.boolean.opBoolean","SPLIT",EDGE,{"disambiguationData":[TD([makeQuery(id+"F5.opExtrude","SWEPT_FACE",FACE,{"disambiguationData":[OSD([sQuery(id+"F4.wireOp",EDGE,"E35.filletArc")])]})])],"derivedFrom":makeQuery(id+"F5.opExtrude","TWEAK_EDGE",EDGE,{"derivedFrom":[subQ0,makeQuery(id+"F4.imprint","IMPRINT",EDGE,{"derivedFrom":subQ1})]})});}
            var Q4;
            {var subQ0=sQuery(id+"F0.wireOp",EDGE,"E25.0");var subQ1=sQuery(id+"F0.wireOp",EDGE,"E25.1");var subQ2=sQuery(id+"F0.wireOp",EDGE,"E25.2");var subQ3=sQuery(id+"F0.wireOp",EDGE,"E25.3");var subQ4=sQuery(id+"F0.wireOp",EDGE,"E25.4");var subQ5=sQuery(id+"F0.wireOp",EDGE,"E25.5");var subQ6=sQuery(id+"F0.wireOp",EDGE,"E25.6");var subQ7=sQuery(id+"F0.wireOp",EDGE,"E25.7");Q4=makeQuery(id+"F8.boolean.opBoolean","INTERSECT",EDGE,{"derivedFrom":[makeQuery(id+"F5.boolean.opBoolean","SPLIT",FACE,{"disambiguationData":[TD([makeQuery(id+"F2.opExtrude","SWEPT_FACE",FACE,{"disambiguationData":[OSD([subQ0])]})])],"derivedFrom":makeQuery(id+"F3.boolean.opBoolean","COPY",FACE,{"derivedFrom":makeQuery(id+"F3.opExtrude","CAP_FACE",FACE,{"disambiguationData":[OSD([subQ0,subQ1,subQ2,subQ3,subQ4,subQ5,subQ6,subQ7])],"isStart":false})})}),makeQuery(id+"F8.opExtrude","SWEPT_FACE",FACE,{"disambiguationData":[OSD([sQuery(id+"F7.wireOp",EDGE,"E67")])]})]});}
            var Q5;
            Q5=makeQuery(id+"F8.boolean.opBoolean","INTERSECT",EDGE,{"disambiguationData":[OD(0.0)],"derivedFrom":[makeQuery(id+"F5.opExtrude","SWEPT_FACE",FACE,{"disambiguationData":[OSD([sQuery(id+"F4.wireOp",EDGE,"E30")])]}),makeQuery(id+"F8.opExtrude","SWEPT_FACE",FACE,{"disambiguationData":[OSD([sQuery(id+"F7.wireOp",EDGE,"E67")])]})]});
            fillet(context, id + "F14", {"entities" : qUnion([Q0, Q1, Q2, Q3, Q4, Q5]), "radius" : 3 * mm, "tangentPropagation" : true, "allowEdgeOverflow" : false});
        }
        {
            var Q0;
            Q0=makeQuery(id+"F1.opExtrude","CAP_EDGE",EDGE,{"disambiguationData":[OSD([sQuery(id+"F0.wireOp",EDGE,"E1.bottom")])],"isStart":false});
            fillet(context, id + "F15", {"entities" : qUnion([Q0]), "radius" : 2 * mm, "tangentPropagation" : true, "allowEdgeOverflow" : false});
        }
        {
            var Q0;
            {var subQ0=sQuery(id+"F0.wireOp",EDGE,"E21.filletArc");var subQ1=sQuery(id+"F0.wireOp",EDGE,"E7");var subQ2=sQuery(id+"F0.wireOp",EDGE,"E6");var subQ3=sQuery(id+"F0.wireOp",EDGE,"E5");var subQ4=sQuery(id+"F0.wireOp",EDGE,"E4");var subQ5=sQuery(id+"F0.wireOp",EDGE,"E22.filletArc");var subQ6=sQuery(id+"F0.wireOp",EDGE,"E1.bottom");var subQ7=sQuery(id+"F0.wireOp",EDGE,"E1.right");var subQ8=sQuery(id+"F0.wireOp",EDGE,"E1.top");var subQ9=sQuery(id+"F0.wireOp",EDGE,"E1.left");var subQ10=sQuery(id+"F0.wireOp",EDGE,"E23.filletArc");var subQ11=sQuery(id+"F0.wireOp",EDGE,"E24.filletArc");Q0=makeQuery(id+"F2.boolean.opBoolean","SPLIT",FACE,{"disambiguationData":[TD([makeQuery(id+"F1.opExtrude","SWEPT_FACE",FACE,{"disambiguationData":[OSD([subQ6])]})])],"derivedFrom":makeQuery(id+"F1.opExtrude","CAP_FACE",FACE,{"disambiguationData":[OSD([subQ6,subQ8,subQ9,subQ7,subQ4,subQ3,subQ2,subQ1,subQ0,subQ5,subQ10,subQ11])],"isStart":true})});}
            var sketch = newSketch(context, id + "F16", { "sketchPlane" : qUnion([Q0])});
            skLineSegment(sketch, "E79", {"start": v(-30.46, 80) * mm, "end": v(-12.46, 98) * mm});
            skLineSegment(sketch, "E80", {"start": v(-12.46, 98) * mm, "end": v(-12.46, 110) * mm});
            skLineSegment(sketch, "E81", {"start": v(17.54, 98) * mm, "end": v(17.54, 97.42) * mm});
            skLineSegment(sketch, "E82", {"start": v(17.54, 98) * mm, "end": v(35.54, 80) * mm});
            skPoint(sketch, "E83.start.orphan", {"position": v(0, 80) * mm});
            skLineSegment(sketch, "E84", {"start": v(17.54, 98) * mm, "end": v(17.54, 110) * mm});
            skArc(sketch, "E85", {"start": v(17.54, 110) * mm, "mid": v(2.54, 125) * mm, "end": v(-12.46, 110) * mm});
            skCircle(sketch, "E86", {"center": v(2.54, 110) * mm, "radius": 6 * mm});
            skCircle(sketch, "E87.MirrorC", {"center": v(2.54, -104.25) * mm, "radius": 6 * mm});
            skLineSegment(sketch, "E88.MirrorCS", {"start": v(17.54, -92.25) * mm, "end": v(17.54, -104.25) * mm});
            skArc(sketch, "E89.MirrorCS", {"start": v(17.54, -104.25) * mm, "mid": v(2.54, -119.25) * mm, "end": v(-12.46, -104.25) * mm});
            skLineSegment(sketch, "E90.MirrorCS", {"start": v(17.54, -92.25) * mm, "end": v(35.54, -74.25) * mm});
            skLineSegment(sketch, "E91.MirrorCS", {"start": v(-30.46, -74.25) * mm, "end": v(-12.46, -92.25) * mm});
            skLineSegment(sketch, "E92.MirrorCS", {"start": v(-12.46, -92.25) * mm, "end": v(-12.46, -104.25) * mm});
            skPoint(sketch, "E93.end.orphan", {"position": v(90, 0) * mm});
            skPoint(sketch, "E93.start.orphan", {"position": v(-90, 0) * mm});
            skSolve(sketch);
        }
        {
            var Q0;
            {var subQ1=sQuery(id+"F16.wireOp",EDGE,"E79");Q0=makeQuery(id+"F16.imprint","IMPRINT",FACE,{"disambiguationData":[TD([[makeQuery(id+"F16.imprint","IMPRINT",EDGE,{"derivedFrom":subQ1}),-1.0]])]});}
            var Q1;
            {var subQ15=sQuery(id+"F0.wireOp",EDGE,"E1.left");Q1=makeQuery(id+"F16.imprint","IMPRINT",FACE,{"disambiguationData":[TD([[makeQuery(id+"F16.imprint","IMPRINT",EDGE,{"derivedFrom":makeQuery(id+"F1.opExtrude","CAP_EDGE",EDGE,{"disambiguationData":[OSD([subQ15])],"isStart":true})}),-1.0]])]});}
            var Q2;
            Q2=makeQuery(id+"F16.imprint","IMPRINT",FACE,{"disambiguationData":[TD([[makeQuery(id+"F16.imprint","IMPRINT",EDGE,{"derivedFrom":sQuery(id+"F16.wireOp",EDGE,"E87.MirrorC")}),1.0]])]});
            var Q3;
            Q3=makeQuery(id+"F2.opExtrude","CAP_FACE",FACE,{"disambiguationData":[OSD([sQuery(id+"F0.wireOp",EDGE,"E12"),sQuery(id+"F0.wireOp",EDGE,"E13"),sQuery(id+"F0.wireOp",EDGE,"E14"),sQuery(id+"F0.wireOp",EDGE,"E15"),sQuery(id+"F0.wireOp",EDGE,"E17.filletArc"),sQuery(id+"F0.wireOp",EDGE,"E18.filletArc"),sQuery(id+"F0.wireOp",EDGE,"E19.filletArc"),sQuery(id+"F0.wireOp",EDGE,"E20.filletArc"),sQuery(id+"F0.wireOp",EDGE,"E25.0"),sQuery(id+"F0.wireOp",EDGE,"E25.1"),sQuery(id+"F0.wireOp",EDGE,"E25.2"),sQuery(id+"F0.wireOp",EDGE,"E25.3"),sQuery(id+"F0.wireOp",EDGE,"E25.4"),sQuery(id+"F0.wireOp",EDGE,"E25.5"),sQuery(id+"F0.wireOp",EDGE,"E25.6"),sQuery(id+"F0.wireOp",EDGE,"E25.7")])],"isStart":false});
            extrude(context, id + "F17", {"entities" : qUnion([Q0, Q1, Q2]), "endBound" : BoundingType.UP_TO_SURFACE, "depth" : 25 * mm, "endBoundEntityFace" : qUnion([Q3]), "offsetDistance" : 25 * mm});
        }
    });
